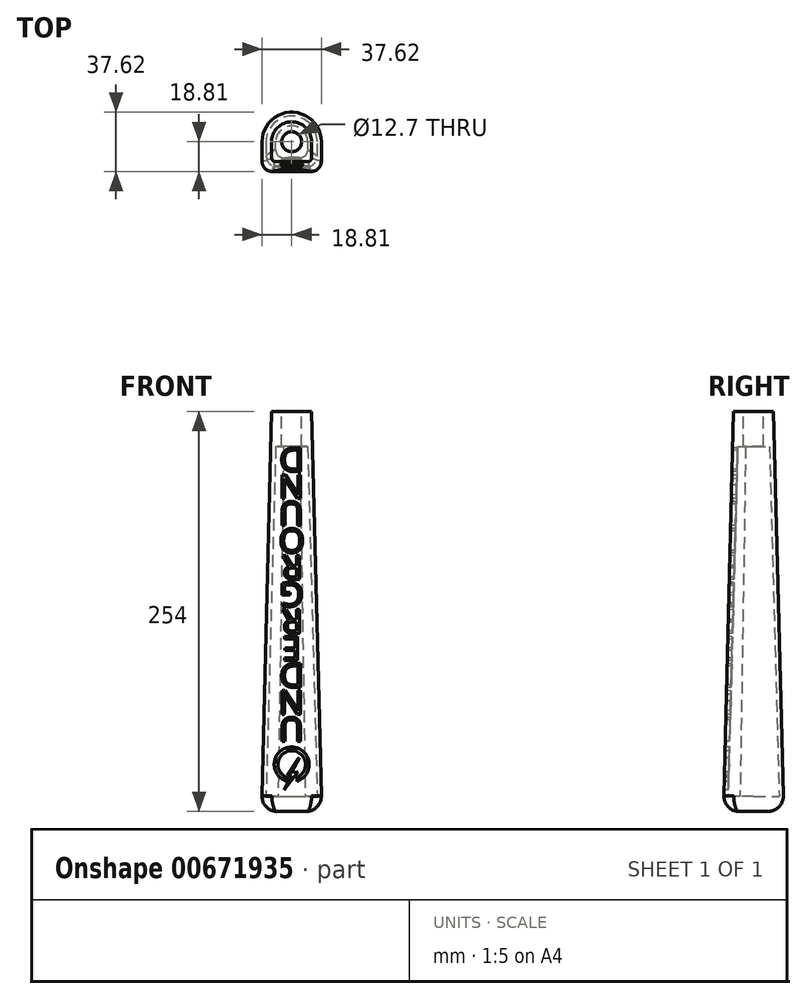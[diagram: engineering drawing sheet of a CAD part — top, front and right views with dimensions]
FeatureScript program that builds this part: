
annotation { "Feature Type Name" : "Feature", "Feature Type Description" : "" }
export const myFeature = defineFeature(function(context is Context, id is Id, definition is map)
    precondition{}
    {
        {
            var Q0;
            Q0=qCreatedBy(makeId("Top.planeOp"),FACE);
            var sketch = newSketch(context, id + "F0", { "sketchPlane" : qUnion([Q0])});
            skLineSegment(sketch, "E0.bottom", {"start": v(0, 19.05) * mm, "end": v(0, 19.05) * mm});
            skLineSegment(sketch, "E0.top", {"start": v(-12.7, -19.05) * mm, "end": v(12.7, -19.05) * mm});
            skLineSegment(sketch, "E0.left", {"start": v(-19.05, 0) * mm, "end": v(-19.05, -12.7) * mm});
            skLineSegment(sketch, "E0.right", {"start": v(19.05, 0) * mm, "end": v(19.05, -12.7) * mm});
            skPoint(sketch, "E1.visualSharp", {"position": v(-19.05, -19.05) * mm});
            skArc(sketch, "E1.filletArc", {"start": v(-19.05, -12.7) * mm, "mid": v(-17.2, -17.2) * mm, "end": v(-12.7, -19.05) * mm});
            skPoint(sketch, "E2.visualSharp", {"position": v(19.05, -19.05) * mm});
            skArc(sketch, "E2.filletArc", {"start": v(12.7, -19.05) * mm, "mid": v(17.2, -17.2) * mm, "end": v(19.05, -12.7) * mm});
            skPoint(sketch, "E3.visualSharp", {"position": v(-19.05, 19.05) * mm});
            skArc(sketch, "E3.filletArc", {"start": v(0, 19.05) * mm, "mid": v(-13.47, 13.47) * mm, "end": v(-19.05, 0) * mm});
            skPoint(sketch, "E4.visualSharp", {"position": v(19.05, 19.05) * mm});
            skArc(sketch, "E4.filletArc", {"start": v(19.05, 0) * mm, "mid": v(13.47, 13.47) * mm, "end": v(0, 19.05) * mm});
            skSolve(sketch);
        }
        {
            var Q0;
            Q0=makeQuery(id+"F0.imprint","IMPRINT",FACE,{"disambiguationData":[TD([[makeQuery(id+"F0.imprint","IMPRINT",EDGE,{"derivedFrom":sQuery(id+"F0.wireOp",EDGE,"E0.top")}),1.0]])]});
            cPlane(context, id + "F1", {"entities" : qUnion([Q0]), "cplaneType" : CPlaneType.OFFSET, "offset" : 254 * mm, "width" : 152.4 * mm, "height" : 152.4 * mm});
        }
        {
            var Q0;
            Q0=qCreatedBy(id+"F1.planeOp",FACE);
            var sketch = newSketch(context, id + "F2", { "sketchPlane" : qUnion([Q0])});
            skLineSegment(sketch, "E5.0", {"start": v(12.7, -10.16) * mm, "end": v(12.7, 0) * mm});
            skLineSegment(sketch, "E5.1", {"start": v(12.7, -12.7) * mm, "end": v(12.7, -12.7) * mm});
            skArc(sketch, "E5.2", {"start": v(0, 12.7) * mm, "mid": v(-8.98, 8.98) * mm, "end": v(-12.7, 0) * mm});
            skLineSegment(sketch, "E5.3", {"start": v(-12.7, 0) * mm, "end": v(-12.7, -10.16) * mm});
            skLineSegment(sketch, "E5.4", {"start": v(-12.7, -12.7) * mm, "end": v(-12.7, -12.7) * mm});
            skArc(sketch, "E5.5", {"start": v(12.7, 0) * mm, "mid": v(8.98, 8.98) * mm, "end": v(0, 12.7) * mm});
            skLineSegment(sketch, "E5.6", {"start": v(-10.16, -12.7) * mm, "end": v(10.16, -12.7) * mm});
            skArc(sketch, "E6.filletArc", {"start": v(-12.7, -10.16) * mm, "mid": v(-11.96, -11.96) * mm, "end": v(-10.16, -12.7) * mm});
            skArc(sketch, "E7.filletArc", {"start": v(10.16, -12.7) * mm, "mid": v(11.96, -11.96) * mm, "end": v(12.7, -10.16) * mm});
            skSolve(sketch);
        }
        {
            var Q0;
            Q0=makeQuery(id+"F0.imprint","IMPRINT",FACE,{"disambiguationData":[TD([[makeQuery(id+"F0.imprint","IMPRINT",EDGE,{"derivedFrom":sQuery(id+"F0.wireOp",EDGE,"E0.top")}),1.0]])]});
            var Q1;
            Q1=makeQuery(id+"F2.imprint","IMPRINT",FACE,{"disambiguationData":[TD([[makeQuery(id+"F2.imprint","IMPRINT",EDGE,{"derivedFrom":sQuery(id+"F2.wireOp",EDGE,"E5.0")}),1.0]])]});
            loft(context, id + "F3", {"sheetProfilesArray" : [{ "sheetProfileEntities" : qUnion([Q0]) }, { "sheetProfileEntities" : qUnion([Q1]) }]});
        }
        {
            var Q0;
            Q0=makeQuery(id+"F3.opLoft","CAP_FACE",FACE,{"disambiguationData":[OSD([makeQuery(id+"F0.imprint","IMPRINT",FACE,{"disambiguationData":[TD([[makeQuery(id+"F0.imprint","IMPRINT",EDGE,{"derivedFrom":sQuery(id+"F0.wireOp",EDGE,"E0.top")}),1.0]])]})])],"isStart":true});
            fillet(context, id + "F4", {"entities" : qUnion([Q0]), "radius" : 9.52 * mm, "tangentPropagation" : true, "allowEdgeOverflow" : false});
        }
        {
            var Q0;
            Q0=makeQuery(id+"F3.opLoft","CAP_FACE",FACE,{"disambiguationData":[OSD([makeQuery(id+"F2.imprint","IMPRINT",FACE,{"disambiguationData":[TD([[makeQuery(id+"F2.imprint","IMPRINT",EDGE,{"derivedFrom":sQuery(id+"F2.wireOp",EDGE,"E5.0")}),1.0]])]})])],"isStart":true});
            var sketch = newSketch(context, id + "F5", { "sketchPlane" : qUnion([Q0])});
            skCircle(sketch, "E8", {"center": v(0, 0) * mm, "radius": 6.35 * mm});
            skSolve(sketch);
        }
        {
            var Q0;
            Q0=makeQuery(id+"F5.imprint","IMPRINT",FACE,{"disambiguationData":[TD([[makeQuery(id+"F5.imprint","IMPRINT",EDGE,{"derivedFrom":sQuery(id+"F5.wireOp",EDGE,"E8")}),1.0]])]});
            var Q1;
            Q1=sQuery(id+"F5.wireOp",EDGE,"E8");
            extrude(context, id + "F6", {"entities" : qUnion([Q0]), "operationType" : NewBodyOperationType.REMOVE, "surfaceEntities" : qUnion([Q1]), "oppositeDirection" : true, "depth" : 22.22 * mm, "offsetDistance" : 25.4 * mm});
        }
        {
            var Q0;
            Q0=makeQuery(id+"F3.opLoft","CAP_FACE",FACE,{"disambiguationData":[OSD([makeQuery(id+"F0.imprint","IMPRINT",FACE,{"disambiguationData":[TD([[makeQuery(id+"F0.imprint","IMPRINT",EDGE,{"derivedFrom":sQuery(id+"F0.wireOp",EDGE,"E0.top")}),1.0]])]})])],"isStart":true});
            cPlane(context, id + "F7", {"entities" : qUnion([Q0]), "cplaneType" : CPlaneType.OFFSET, "offset" : 9.52 * mm, "oppositeDirection" : true, "width" : 152.4 * mm, "height" : 152.4 * mm});
        }
        {
            var Q0;
            Q0=qCreatedBy(id+"F1.planeOp",FACE);
            cPlane(context, id + "F8", {"entities" : qUnion([Q0]), "cplaneType" : CPlaneType.OFFSET, "offset" : 22.22 * mm, "oppositeDirection" : true, "width" : 152.4 * mm, "height" : 152.4 * mm});
        }
        {
            var Q0;
            Q0=qCreatedBy(id+"F7.planeOp",FACE);
            var sketch = newSketch(context, id + "F9", { "sketchPlane" : qUnion([Q0])});
            skLineSegment(sketch, "E9.0", {"start": v(16.27, 8.65) * mm, "end": v(16.27, 0) * mm});
            skLineSegment(sketch, "E9.1", {"start": v(-8.65, 16.27) * mm, "end": v(8.65, 16.27) * mm});
            skLineSegment(sketch, "E9.2", {"start": v(-16.27, 0) * mm, "end": v(-16.27, 8.65) * mm});
            skArc(sketch, "E9.3", {"start": v(16.27, 0) * mm, "mid": v(0, -16.27) * mm, "end": v(-16.27, 0) * mm});
            skPoint(sketch, "E10.visualSharp", {"position": v(-16.27, 16.27) * mm});
            skArc(sketch, "E10.filletArc", {"start": v(-8.65, 16.27) * mm, "mid": v(-14.03, 14.03) * mm, "end": v(-16.27, 8.65) * mm});
            skPoint(sketch, "E11.visualSharp", {"position": v(16.27, 16.27) * mm});
            skArc(sketch, "E11.filletArc", {"start": v(16.27, 8.65) * mm, "mid": v(14.03, 14.03) * mm, "end": v(8.65, 16.27) * mm});
            skSolve(sketch);
        }
        {
            var Q0;
            Q0=qCreatedBy(id+"F8.planeOp",FACE);
            var sketch = newSketch(context, id + "F10", { "sketchPlane" : qUnion([Q0])});
            skArc(sketch, "E12.0", {"start": v(-10.16, 0) * mm, "mid": v(0, 10.16) * mm, "end": v(10.16, 0) * mm});
            skLineSegment(sketch, "E12.1", {"start": v(-10.16, -5.08) * mm, "end": v(-10.16, 0) * mm});
            skLineSegment(sketch, "E12.2", {"start": v(5.08, -10.16) * mm, "end": v(-5.08, -10.16) * mm});
            skLineSegment(sketch, "E12.3", {"start": v(10.16, 0) * mm, "end": v(10.16, -5.08) * mm});
            skPoint(sketch, "E13.visualSharp", {"position": v(10.16, -10.16) * mm});
            skArc(sketch, "E13.filletArc", {"start": v(5.08, -10.16) * mm, "mid": v(8.67, -8.67) * mm, "end": v(10.16, -5.08) * mm});
            skPoint(sketch, "E14.visualSharp", {"position": v(-10.16, -10.16) * mm});
            skArc(sketch, "E14.filletArc", {"start": v(-10.16, -5.08) * mm, "mid": v(-8.67, -8.67) * mm, "end": v(-5.08, -10.16) * mm});
            skSolve(sketch);
        }
        {
            var Q1;
            Q1 = qSketchRegion(id + "F10", true);
            var Q2;
            Q2 = qSketchRegion(id + "F9", true);
            loft(context, id + "F11", {"operationType" : NewBodyOperationType.REMOVE, "sheetProfilesArray" : [{ "sheetProfileEntities" : qUnion([Q1]) }, { "sheetProfileEntities" : qUnion([Q2]) }]});
        }
        {
            var Q0;
            Q0=makeQuery(id+"F3.opLoft","SWEPT_FACE",FACE,{"disambiguationData":[OSD([sQuery(id+"F0.wireOp",EDGE,"E0.top"),sQuery(id+"F0.wireOp",EDGE,"E1.filletArc"),sQuery(id+"F0.wireOp",EDGE,"E2.filletArc"),sQuery(id+"F2.wireOp",EDGE,"E5.6"),sQuery(id+"F2.wireOp",EDGE,"E6.filletArc"),sQuery(id+"F2.wireOp",EDGE,"E7.filletArc")])]});
            var sketch = newSketch(context, id + "F12", { "sketchPlane" : qUnion([Q0])});
            skLineSegment(sketch, "E15", {"start": v(-4.76, 13.2) * mm, "end": v(2.1, 22.24) * mm});
            skLineSegment(sketch, "E16", {"start": v(3.88, 24.59) * mm, "end": v(0, 24.32) * mm});
            skLineSegment(sketch, "E17", {"start": v(0, 24.32) * mm, "end": v(4.95, 33.64) * mm});
            skLineSegment(sketch, "E18", {"start": v(4.95, 33.64) * mm, "end": v(-2.84, 22.46) * mm});
            skLineSegment(sketch, "E19", {"start": v(-2.84, 22.46) * mm, "end": v(0, 22.46) * mm});
            skLineSegment(sketch, "E20", {"start": v(0, 22.46) * mm, "end": v(-4.76, 13.2) * mm});
            skLineSegment(sketch, "E21", {"start": v(-3.3, 21.17) * mm, "end": v(-3.3, 18.71) * mm});
            skArc(sketch, "E22", {"start": v(3.3, 18.71) * mm, "mid": v(8.27, 21.9) * mm, "end": v(10.9, 27.18) * mm});
            skArc(sketch, "E23", {"start": v(3.3, 21.17) * mm, "mid": v(0, 38.11) * mm, "end": v(-3.3, 21.17) * mm});
            skLineSegment(sketch, "E24", {"start": v(3.3, 18.71) * mm, "end": v(3.3, 21.15) * mm});
            skPoint(sketch, "E25.orphan", {"position": v(-22.4, 18.71) * mm});
            skArc(sketch, "E26.trimOffspring", {"start": v(10.9, 27.18) * mm, "mid": v(-5.69, 38.86) * mm, "end": v(-3.3, 18.71) * mm});
            skPoint(sketch, "E27.orphan", {"position": v(-12.6, 9.29) * mm});
            skPoint(sketch, "E28.orphan", {"position": v(-10.16, 253.6) * mm});
            skPoint(sketch, "E29.orphan", {"position": v(10.16, 253.6) * mm});
            skPoint(sketch, "E30.orphan", {"position": v(12.6, 9.29) * mm});
            skPoint(sketch, "E31.startSnap0", {"position": v(1.94, 24.46) * mm});
            skPoint(sketch, "E32.orphan", {"position": v(1.94, 23.57) * mm});
            skPoint(sketch, "E33.orphan", {"position": v(-8.19, 21.17) * mm});
            skPoint(sketch, "E34.orphan", {"position": v(-3.3, 21.17) * mm});
            skLineSegment(sketch, "E35.trimOffspring", {"start": v(2.94, 23.35) * mm, "end": v(3.88, 24.59) * mm});
            skPoint(sketch, "E36.orphan", {"position": v(3.3, 21.17) * mm});
            skLineSegment(sketch, "E37", {"start": v(3.3, 21.15) * mm, "end": v(3.3, 21.17) * mm});
            skLineSegment(sketch, "E38", {"start": v(-3.3, 21.17) * mm, "end": v(-3.3, 21.17) * mm});
            skLineSegment(sketch, "E39", {"start": v(2.94, 23.35) * mm, "end": v(2.1, 22.24) * mm});
            skSolve(sketch);
        }
        {
            var Q0;
            {var subQ0=sQuery(id+"F12.wireOp",EDGE,"E26.trimOffspring");Q0=makeQuery(id+"F12.imprint","IMPRINT",FACE,{"disambiguationData":[TD([[makeQuery(id+"F12.imprint","IMPRINT",EDGE,{"derivedFrom":subQ0}),-1.0]])]});}
            var sketch = newSketch(context, id + "F13", { "sketchPlane" : qUnion([Q0])});
            skText(sketch, "E40", { "text": "U", "fontName": "OpenSans-Regular.ttf"});
            const initialGuessF13  = {"E40": [0.00743, 0.05912, -1, 0, 0.01524]};
            skSetInitialGuess(sketch, initialGuessF13);
            skSolve(sketch);
        }
        {
            var Q0;
            Q0=makeQuery(id+"F13.imprint","IMPRINT",FACE,{"disambiguationData":[TD([[makeQuery(id+"F13.imprint","IMPRINT",EDGE,{"derivedFrom":sQuery(id+"F13.wireOp",EDGE,"E40.sketch_text.stroke-0")}),1.0]])]});
            var sketch = newSketch(context, id + "F14", { "sketchPlane" : qUnion([Q0])});
            skText(sketch, "E41", { "text": "N", "fontName": "OpenSans-Regular.ttf"});
            skText(sketch, "E42", { "text": "D", "fontName": "OpenSans-Regular.ttf"});
            skText(sketch, "E43", { "text": "E", "fontName": "OpenSans-Regular.ttf"});
            skText(sketch, "E44", { "text": "R", "fontName": "OpenSans-Regular.ttf"});
            skText(sketch, "E45", { "text": "G", "fontName": "OpenSans-Regular.ttf"});
            skText(sketch, "E46", { "text": "R", "fontName": "OpenSans-Regular.ttf"});
            skText(sketch, "E47", { "text": "O", "fontName": "OpenSans-Regular.ttf"});
            skText(sketch, "E48", { "text": "U", "fontName": "OpenSans-Regular.ttf"});
            skText(sketch, "E49", { "text": "N", "fontName": "OpenSans-Regular.ttf"});
            skText(sketch, "E50", { "text": "D", "fontName": "OpenSans-Regular.ttf"});
            const initialGuessF14  = {"E41": [0.00763, 0.07626, -1, 0, 0.01524], "E42": [0.00776, 0.0934, -1, 0, 0.01524], "E43": [0.00594, 0.11055, -1, 0, 0.01524], "E44": [0.00705, 0.1277, -1, 0, 0.01524], "E45": [0.00762, 0.14484, -1, 0, 0.01524], "E46": [0.00705, 0.16199, -1, 0, 0.01524], "E47": [0.00828, 0.17913, -1, 0, 0.01524], "E48": [0.00743, 0.19628, -1, 0, 0.01524], "E49": [0.00782, 0.21342, -1, 0, 0.01524], "E50": [0.00776, 0.23057, -1, 0, 0.01524]};
            skSetInitialGuess(sketch, initialGuessF14);
            skSolve(sketch);
        }
        {
            var Q0;
            Q0 = qSketchRegion(id + "F14", true);
            var Q1;
            Q1 = qSketchRegion(id + "F13", true);
            extrude(context, id + "F15", {"entities" : qUnion([Q0, Q1]), "operationType" : NewBodyOperationType.REMOVE, "oppositeDirection" : true, "depth" : 5.08 * mm, "offsetDistance" : 25.4 * mm});
        }
        {
            var Q0;
            Q0=makeQuery(id+"F12.imprint","IMPRINT",FACE,{"disambiguationData":[TD([[makeQuery(id+"F12.imprint","IMPRINT",EDGE,{"derivedFrom":sQuery(id+"F12.wireOp",EDGE,"E21")}),-1.0]])]});
            var Q1;
            Q1=makeQuery(id+"F12.imprint","IMPRINT",FACE,{"disambiguationData":[TD([[makeQuery(id+"F12.imprint","IMPRINT",EDGE,{"derivedFrom":sQuery(id+"F12.wireOp",EDGE,"E15")}),1.0]])]});
            extrude(context, id + "F16", {"entities" : qUnion([Q0, Q1]), "operationType" : NewBodyOperationType.REMOVE, "oppositeDirection" : true, "depth" : 5.08 * mm, "offsetDistance" : 25.4 * mm});
        }
    });
